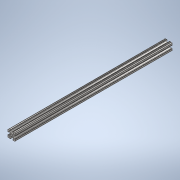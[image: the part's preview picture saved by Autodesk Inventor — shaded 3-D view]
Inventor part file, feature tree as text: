
AUTODESK INVENTOR PART (.ipt)
format: ipt  version: 2020 (Build 240168000, 168)  size: 241,664 bytes
history: native  units: in
note: dims shown in document units (in); Inventor stores cm internally (conversion verified against a paired STEP export)
features: extrude x1, sketch x1
ambient origin geometry x8: Origin, YZ Plane, XZ Plane, XY Plane, X Axis, Y Axis, Z Axis, Center Point
bodies: Solid1 (feature_tree)
feature tree (2):
  extrude  "Extrusion1"  [1 undecoded]
  sketch  "Sketch1"  dims[d0=21.0in d1=0.0in]
note: 1 required parameter value undecoded (feature->parameter linkage not recoverable at this tier; creation-order binding heuristic only, values carry confidence <= 0.55)
